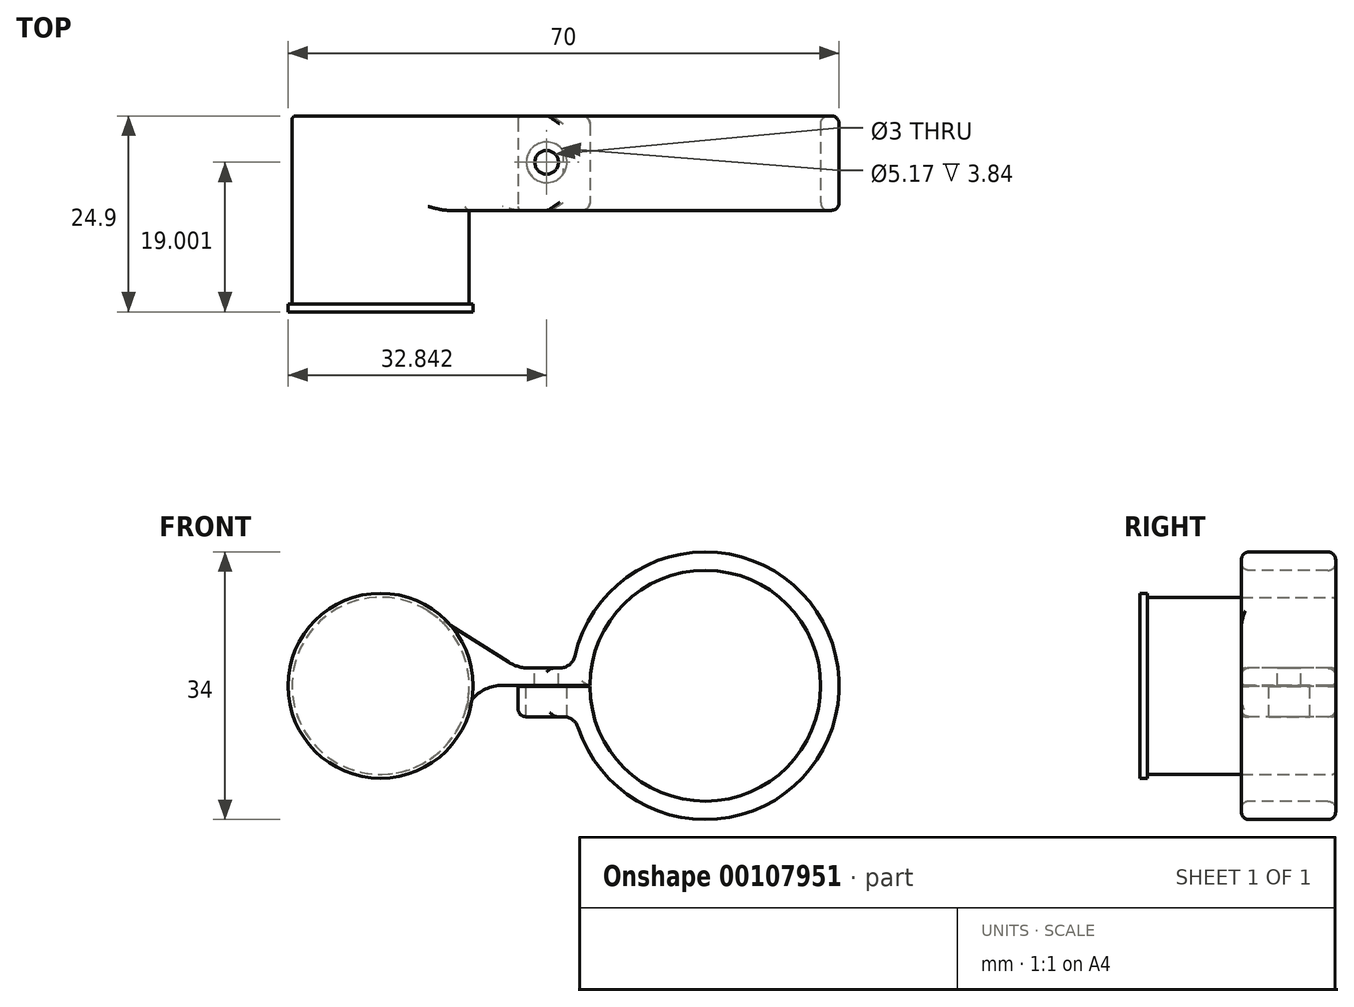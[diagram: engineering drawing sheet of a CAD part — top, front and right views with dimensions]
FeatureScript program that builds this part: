
annotation { "Feature Type Name" : "Feature", "Feature Type Description" : "" }
export const myFeature = defineFeature(function(context is Context, id is Id, definition is map)
    precondition{}
    {
        {
            var Q0;
            Q0=qCreatedBy(makeId("Front.planeOp"),FACE);
            var sketch = newSketch(context, id + "F0", { "sketchPlane" : qUnion([Q0])});
            skCircle(sketch, "E0", {"center": v(0, 0) * mm, "radius": 11.25 * mm});
            skSolve(sketch);
        }
        {
            var Q0;
            Q0 = qSketchRegion(id + "F0", true);
            extrude(context, id + "F1", {"entities" : qUnion([Q0]), "depth" : 11.9 * mm});
        }
        {
            var Q0;
            Q0=makeQuery(id+"F1.opExtrude","CAP_FACE",FACE,{"disambiguationData":[OSD([sQuery(id+"F0.wireOp",EDGE,"E0")])],"isStart":false});
            var sketch = newSketch(context, id + "F2", { "sketchPlane" : qUnion([Q0])});
            skCircle(sketch, "E1", {"center": v(0, 0) * mm, "radius": 11.75 * mm});
            skSolve(sketch);
        }
        {
            var Q0;
            Q0 = qSketchRegion(id + "F2", true);
            extrude(context, id + "F3", {"entities" : qUnion([Q0]), "operationType" : NewBodyOperationType.ADD, "depth" : 1 * mm});
        }
        {
            var Q0;
            Q0=makeQuery(id+"F1.opExtrude","CAP_FACE",FACE,{"disambiguationData":[OSD([sQuery(id+"F0.wireOp",EDGE,"E0")])],"isStart":true});
            var sketch = newSketch(context, id + "F4", { "sketchPlane" : qUnion([Q0])});
            skArc(sketch, "E2", {"start": v(-24.68, 3.8) * mm, "mid": v(-58.23, 0.78) * mm, "end": v(-25.1, -5.3) * mm});
            skArc(sketch, "E3.0", {"start": v(-26.6, 0.06) * mm, "mid": v(-55.9, 0.01) * mm, "end": v(-26.6, -0.08) * mm});
            skCircle(sketch, "E4", {"center": v(0, 0) * mm, "radius": 11.25 * mm});
            skLineSegment(sketch, "E5", {"start": v(-11.25, 0.06) * mm, "end": v(-26.6, 0.06) * mm});
            skLineSegment(sketch, "E6", {"start": v(-6.03, 9.5) * mm, "end": v(-16.23, 3.02) * mm});
            skLineSegment(sketch, "E7", {"start": v(-18.9, 2.24) * mm, "end": v(-22.73, 2.24) * mm});
            skLineSegment(sketch, "E8", {"start": v(-18.45, -3.92) * mm, "end": v(-23.2, -3.92) * mm});
            skLineSegment(sketch, "E9", {"start": v(0, 0) * mm, "end": v(-41.25, 0) * mm, "construction": true});
            skPoint(sketch, "E10.visualSharp", {"position": v(-17.45, 2.24) * mm});
            skArc(sketch, "E10.filletArc", {"start": v(-18.9, 2.24) * mm, "mid": v(-17.51, 2.44) * mm, "end": v(-16.23, 3.02) * mm});
            skPoint(sketch, "E11.visualSharp", {"position": v(-24.4, 2.24) * mm});
            skArc(sketch, "E11.filletArc", {"start": v(-24.68, 3.8) * mm, "mid": v(-23.98, 2.68) * mm, "end": v(-22.73, 2.24) * mm});
            skLineSegment(sketch, "E12", {"start": v(-26.6, -0.08) * mm, "end": v(-17.45, -0.08) * mm});
            skLineSegment(sketch, "E13", {"start": v(-17.45, -0.08) * mm, "end": v(-17.45, -2.92) * mm});
            skPoint(sketch, "E14.visualSharp", {"position": v(-24.7, -3.92) * mm});
            skArc(sketch, "E14.filletArc", {"start": v(-23.2, -3.92) * mm, "mid": v(-24.37, -4.3) * mm, "end": v(-25.1, -5.3) * mm});
            skPoint(sketch, "E15.visualSharp", {"position": v(-17.45, -3.92) * mm});
            skArc(sketch, "E15.filletArc", {"start": v(-18.45, -3.92) * mm, "mid": v(-17.75, -3.63) * mm, "end": v(-17.45, -2.92) * mm});
            skSolve(sketch);
        }
        {
            var Q0;
            {var subQ0=sQuery(id+"F4.wireOp",EDGE,"E4");var subQ1=makeQuery(id+"F4.imprint","INTERSECT",VERTEX,{"derivedFrom":[subQ0,sQuery(id+"F4.wireOp",EDGE,"E5")]});Q0=makeQuery(id+"F4.imprint","IMPRINT",FACE,{"disambiguationData":[TD([[makeQuery(id+"F4.imprint","IMPRINT",EDGE,{"disambiguationData":[TD([[subQ1,-1.0]])],"derivedFrom":subQ0}),-1.0]])]});}
            var Q1;
            Q1=makeQuery(id+"F4.imprint","IMPRINT",FACE,{"disambiguationData":[TD([[makeQuery(id+"F4.imprint","IMPRINT",EDGE,{"derivedFrom":sQuery(id+"F4.wireOp",EDGE,"E2")}),1.0]])]});
            extrude(context, id + "F5", {"entities" : qUnion([Q0, Q1]), "operationType" : NewBodyOperationType.ADD, "depth" : 12 * mm});
        }
        {
            var Q0;
            Q0=makeQuery(id+"F5.opExtrude","SWEPT_FACE",FACE,{"disambiguationData":[OSD([sQuery(id+"F4.wireOp",EDGE,"E7")])]});
            var sketch = newSketch(context, id + "F6", { "sketchPlane" : qUnion([Q0])});
            skCircle(sketch, "E16", {"center": v(21.1, 6.1) * mm, "radius": 1.5 * mm});
            skSolve(sketch);
        }
        {
            var Q0;
            Q0 = qSketchRegion(id + "F6", true);
            extrude(context, id + "F7", {"entities" : qUnion([Q0]), "operationType" : NewBodyOperationType.REMOVE, "endBound" : BoundingType.THROUGH_ALL, "oppositeDirection" : true, "depth" : 25 * mm});
        }
        {
            var Q0;
            Q0=makeQuery(id+"F5.opExtrude","SWEPT_FACE",FACE,{"disambiguationData":[OSD([sQuery(id+"F4.wireOp",EDGE,"E12")])]});
            var sketch = newSketch(context, id + "F8", { "sketchPlane" : qUnion([Q0])});
            skCircle(sketch, "E17", {"center": v(21.1, 6.1) * mm, "radius": 2.58 * mm});
            skSolve(sketch);
        }
        {
            var Q0;
            Q0 = qSketchRegion(id + "F8", true);
            var Q1;
            Q1=makeQuery(id+"F5.opExtrude","SWEPT_FACE",FACE,{"disambiguationData":[OSD([sQuery(id+"F4.wireOp",EDGE,"E8")])]});
            extrude(context, id + "F9", {"entities" : qUnion([Q0]), "operationType" : NewBodyOperationType.REMOVE, "endBound" : BoundingType.UP_TO_SURFACE, "oppositeDirection" : true, "endBoundEntityFace" : qUnion([Q1]), "depth" : 25 * mm});
        }
        {
            var Q0;
            Q0=makeQuery(id+"F5.opExtrude","SWEPT_EDGE",EDGE,{"disambiguationData":[OSD([sQuery(id+"F4.wireOp",EDGE,"E4"),sQuery(id+"F4.wireOp",EDGE,"E5")])]});
            fillet(context, id + "F10", {"entities" : qUnion([Q0]), "radius" : 5 * mm, "tangentPropagation" : true, "allowEdgeOverflow" : false});
        }
        {
            var Q0;
            Q0=makeQuery(id+"F5.opExtrude","CAP_EDGE",EDGE,{"disambiguationData":[OSD([sQuery(id+"F4.wireOp",EDGE,"E6")])],"isStart":true});
            var Q1;
            Q1=makeQuery(id+"F5.opExtrude","CAP_EDGE",EDGE,{"disambiguationData":[OSD([sQuery(id+"F4.wireOp",EDGE,"E10.filletArc")])],"isStart":true});
            var Q2;
            Q2=makeQuery(id+"F5.opExtrude","CAP_EDGE",EDGE,{"disambiguationData":[OSD([sQuery(id+"F4.wireOp",EDGE,"E7")])],"isStart":true});
            var Q3;
            {var subQ0=sQuery(id+"F4.wireOp",EDGE,"E5");var subQ1=sQuery(id+"F4.wireOp",EDGE,"E4");Q3=makeQuery(id+"F10.opFillet","BLEND_EDGE",EDGE,{"blendedFrom":[makeQuery(id+"F5.opExtrude","SWEPT_EDGE",EDGE,{"disambiguationData":[OSD([subQ1,subQ0])]}),makeQuery(id+"F5.opExtrude","CAP_FACE",FACE,{"disambiguationData":[OSD([sQuery(id+"F4.wireOp",EDGE,"E2"),sQuery(id+"F4.wireOp",EDGE,"E3.0"),subQ1,subQ0,sQuery(id+"F4.wireOp",EDGE,"E6"),sQuery(id+"F4.wireOp",EDGE,"E7"),sQuery(id+"F4.wireOp",EDGE,"E8"),sQuery(id+"F4.wireOp",EDGE,"E10.filletArc"),sQuery(id+"F4.wireOp",EDGE,"E11.filletArc"),sQuery(id+"F4.wireOp",EDGE,"E12"),sQuery(id+"F4.wireOp",EDGE,"E13"),sQuery(id+"F4.wireOp",EDGE,"E14.filletArc"),sQuery(id+"F4.wireOp",EDGE,"E15.filletArc")])],"isStart":true})],"blendedInto":[makeQuery(id+"F5.opExtrude","CAP_FACE",FACE,{"disambiguationData":[OSD([sQuery(id+"F4.wireOp",EDGE,"E2"),sQuery(id+"F4.wireOp",EDGE,"E3.0"),subQ1,subQ0,sQuery(id+"F4.wireOp",EDGE,"E6"),sQuery(id+"F4.wireOp",EDGE,"E7"),sQuery(id+"F4.wireOp",EDGE,"E8"),sQuery(id+"F4.wireOp",EDGE,"E10.filletArc"),sQuery(id+"F4.wireOp",EDGE,"E11.filletArc"),sQuery(id+"F4.wireOp",EDGE,"E12"),sQuery(id+"F4.wireOp",EDGE,"E13"),sQuery(id+"F4.wireOp",EDGE,"E14.filletArc"),sQuery(id+"F4.wireOp",EDGE,"E15.filletArc")])],"isStart":true})]});}
            var Q4;
            Q4=makeQuery(id+"F5.opExtrude","CAP_EDGE",EDGE,{"disambiguationData":[OSD([sQuery(id+"F4.wireOp",EDGE,"E11.filletArc")])],"isStart":true});
            var Q5;
            Q5=makeQuery(id+"F5.opExtrude","CAP_EDGE",EDGE,{"disambiguationData":[OSD([sQuery(id+"F4.wireOp",EDGE,"E8")])],"isStart":true});
            var Q6;
            Q6=makeQuery(id+"F5.opExtrude","CAP_EDGE",EDGE,{"disambiguationData":[OSD([sQuery(id+"F4.wireOp",EDGE,"E15.filletArc")])],"isStart":true});
            var Q7;
            Q7=makeQuery(id+"F5.opExtrude","CAP_EDGE",EDGE,{"disambiguationData":[OSD([sQuery(id+"F4.wireOp",EDGE,"E13")])],"isStart":true});
            var Q8;
            Q8=makeQuery(id+"F5.opExtrude","CAP_EDGE",EDGE,{"disambiguationData":[OSD([sQuery(id+"F4.wireOp",EDGE,"E14.filletArc")])],"isStart":true});
            var Q9;
            Q9=makeQuery(id+"F5.opExtrude","CAP_EDGE",EDGE,{"disambiguationData":[OSD([sQuery(id+"F4.wireOp",EDGE,"E6")])],"isStart":false});
            var Q10;
            {var subQ0=sQuery(id+"F4.wireOp",EDGE,"E5");var subQ1=sQuery(id+"F4.wireOp",EDGE,"E4");Q10=makeQuery(id+"F10.opFillet","BLEND_EDGE",EDGE,{"blendedFrom":[makeQuery(id+"F5.opExtrude","SWEPT_EDGE",EDGE,{"disambiguationData":[OSD([subQ1,subQ0])]}),makeQuery(id+"F5.opExtrude","CAP_FACE",FACE,{"disambiguationData":[OSD([sQuery(id+"F4.wireOp",EDGE,"E2"),sQuery(id+"F4.wireOp",EDGE,"E3.0"),subQ1,subQ0,sQuery(id+"F4.wireOp",EDGE,"E6"),sQuery(id+"F4.wireOp",EDGE,"E7"),sQuery(id+"F4.wireOp",EDGE,"E8"),sQuery(id+"F4.wireOp",EDGE,"E10.filletArc"),sQuery(id+"F4.wireOp",EDGE,"E11.filletArc"),sQuery(id+"F4.wireOp",EDGE,"E12"),sQuery(id+"F4.wireOp",EDGE,"E13"),sQuery(id+"F4.wireOp",EDGE,"E14.filletArc"),sQuery(id+"F4.wireOp",EDGE,"E15.filletArc")])],"isStart":false})],"blendedInto":[makeQuery(id+"F5.opExtrude","CAP_FACE",FACE,{"disambiguationData":[OSD([sQuery(id+"F4.wireOp",EDGE,"E2"),sQuery(id+"F4.wireOp",EDGE,"E3.0"),subQ1,subQ0,sQuery(id+"F4.wireOp",EDGE,"E6"),sQuery(id+"F4.wireOp",EDGE,"E7"),sQuery(id+"F4.wireOp",EDGE,"E8"),sQuery(id+"F4.wireOp",EDGE,"E10.filletArc"),sQuery(id+"F4.wireOp",EDGE,"E11.filletArc"),sQuery(id+"F4.wireOp",EDGE,"E12"),sQuery(id+"F4.wireOp",EDGE,"E13"),sQuery(id+"F4.wireOp",EDGE,"E14.filletArc"),sQuery(id+"F4.wireOp",EDGE,"E15.filletArc")])],"isStart":false})]});}
            var Q11;
            Q11=makeQuery(id+"F5.opExtrude","CAP_EDGE",EDGE,{"disambiguationData":[OSD([sQuery(id+"F4.wireOp",EDGE,"E5")])],"isStart":false});
            var Q12;
            Q12=makeQuery(id+"F5.opExtrude","CAP_EDGE",EDGE,{"disambiguationData":[OSD([sQuery(id+"F4.wireOp",EDGE,"E10.filletArc")])],"isStart":false});
            var Q13;
            Q13=makeQuery(id+"F5.opExtrude","CAP_EDGE",EDGE,{"disambiguationData":[OSD([sQuery(id+"F4.wireOp",EDGE,"E7")])],"isStart":false});
            var Q14;
            Q14=makeQuery(id+"F5.opExtrude","CAP_EDGE",EDGE,{"disambiguationData":[OSD([sQuery(id+"F4.wireOp",EDGE,"E11.filletArc")])],"isStart":false});
            var Q15;
            Q15=makeQuery(id+"F5.opExtrude","CAP_EDGE",EDGE,{"disambiguationData":[OSD([sQuery(id+"F4.wireOp",EDGE,"E14.filletArc")])],"isStart":false});
            var Q16;
            Q16=makeQuery(id+"F5.opExtrude","CAP_EDGE",EDGE,{"disambiguationData":[OSD([sQuery(id+"F4.wireOp",EDGE,"E8")])],"isStart":false});
            var Q17;
            Q17=makeQuery(id+"F5.opExtrude","CAP_EDGE",EDGE,{"disambiguationData":[OSD([sQuery(id+"F4.wireOp",EDGE,"E15.filletArc")])],"isStart":false});
            var Q18;
            Q18=makeQuery(id+"F5.opExtrude","CAP_EDGE",EDGE,{"disambiguationData":[OSD([sQuery(id+"F4.wireOp",EDGE,"E13")])],"isStart":false});
            var Q19;
            Q19=makeQuery(id+"F5.opExtrude","CAP_EDGE",EDGE,{"disambiguationData":[OSD([sQuery(id+"F4.wireOp",EDGE,"E4")])],"isStart":false});
            fillet(context, id + "F11", {"entities" : qUnion([Q0, Q1, Q2, Q3, Q4, Q5, Q6, Q7, Q8, Q9, Q10, Q11, Q12, Q13, Q14, Q15, Q16, Q17, Q18, Q19]), "radius" : .5 * mm, "allowEdgeOverflow" : false});
        }
        {
            var Q0;
            Q0=makeQuery(id+"F5.opExtrude","CAP_EDGE",EDGE,{"disambiguationData":[OSD([sQuery(id+"F4.wireOp",EDGE,"E2")])],"isStart":false});
            var Q1;
            Q1=makeQuery(id+"F5.opExtrude","CAP_EDGE",EDGE,{"disambiguationData":[OSD([sQuery(id+"F4.wireOp",EDGE,"E3.0")])],"isStart":false});
            var Q2;
            Q2=makeQuery(id+"F5.opExtrude","CAP_EDGE",EDGE,{"disambiguationData":[OSD([sQuery(id+"F4.wireOp",EDGE,"E2")])],"isStart":true});
            var Q3;
            Q3=makeQuery(id+"F5.opExtrude","CAP_EDGE",EDGE,{"disambiguationData":[OSD([sQuery(id+"F4.wireOp",EDGE,"E3.0")])],"isStart":true});
            fillet(context, id + "F12", {"entities" : qUnion([Q0, Q1, Q2, Q3]), "radius" : 1 * mm, "allowEdgeOverflow" : false});
        }
    });
